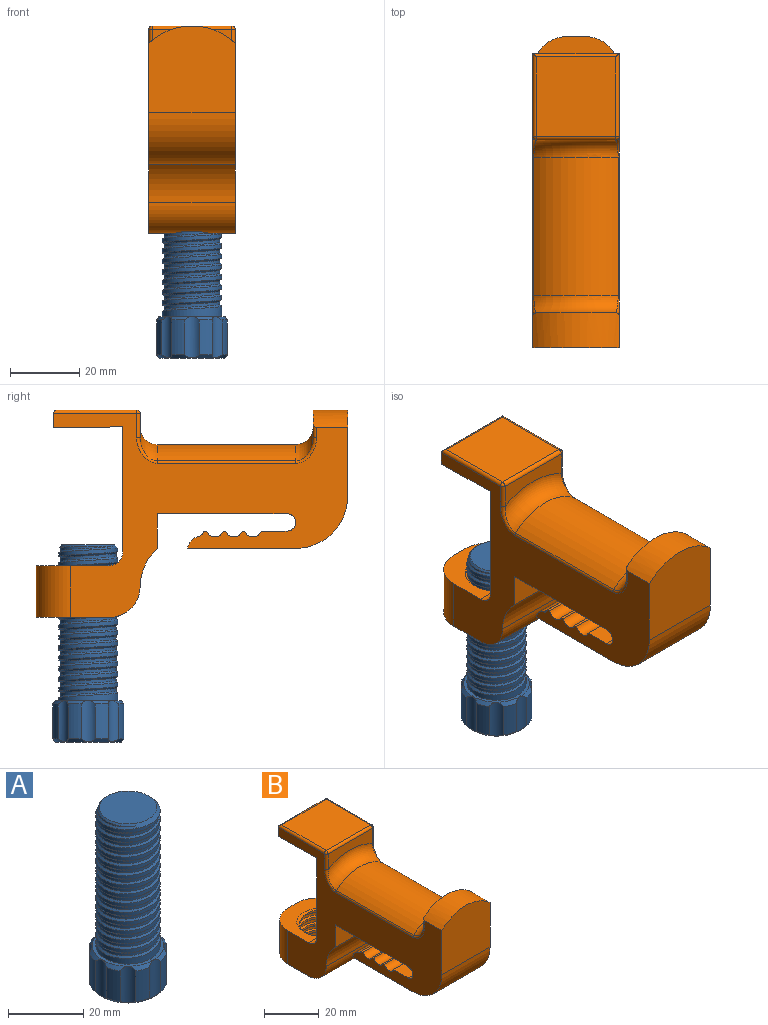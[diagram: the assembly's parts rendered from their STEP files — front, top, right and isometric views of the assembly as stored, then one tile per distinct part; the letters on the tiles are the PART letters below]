
ASSEMBLY  parts=2 mates=1
PART A: 41 faces, bbox 20.9x20.9x57.4 mm
  f0: cylinder r=10.45mm len=10mm, axis (0,0,-1), area 41mm2, adj f7,f27,f33,f40
  f1: cylinder r=10.45mm len=10mm, axis (0,0,-1), area 41mm2, adj f8,f14,f39,f40
  f2: cylinder r=10.45mm len=10mm, axis (0,0,-1), area 41mm2, adj f9,f15,f38,f39
  f3: cylinder r=10.45mm len=10mm, axis (0,0,-1), area 41mm2, adj f10,f16,f37,f38
  f4: cylinder r=10.45mm len=10mm, axis (0,0,-1), area 41mm2, adj f11,f17,f36,f37
  f5: cylinder r=10.45mm len=10mm, axis (0,0,-1), area 41mm2, adj f12,f18,f35,f36
  f6: cylinder r=10.45mm len=10mm, axis (0,0,-1), area 41mm2, adj f13,f19,f34,f35
  f7: cone r=10.45mm half-angle=43.5deg, axis (0,0,1), area 7mm2, adj f0,f24,f33,f40
  f8: cone r=10.45mm half-angle=43.5deg, axis (0,0,1), area 7mm2, adj f1,f24,f39,f40
  f9: cone r=10.45mm half-angle=43.5deg, axis (0,0,1), area 7mm2, adj f2,f24,f38,f39
  f10: cone r=10.45mm half-angle=43.5deg, axis (0,0,1), area 7mm2, adj f3,f24,f37,f38
  f11: cone r=10.45mm half-angle=43.5deg, axis (0,0,1), area 7mm2, adj f4,f24,f36,f37
  f12: cone r=10.45mm half-angle=43.5deg, axis (0,0,1), area 7mm2, adj f5,f24,f35,f36
  f13: cone r=10.45mm half-angle=43.5deg, axis (0,0,1), area 7mm2, adj f6,f24,f34,f35
  f14: cone r=10.45mm half-angle=43.5deg, axis (0,0,-1), area 7mm2, adj f1,f23,f39,f40
  f15: cone r=10.45mm half-angle=43.5deg, axis (0,0,-1), area 7mm2, adj f2,f23,f38,f39
  f16: cone r=10.45mm half-angle=43.5deg, axis (0,0,-1), area 7mm2, adj f3,f23,f37,f38
  f17: cone r=10.45mm half-angle=43.5deg, axis (0,0,-1), area 7mm2, adj f4,f23,f36,f37
  f18: cone r=10.45mm half-angle=43.5deg, axis (0,0,-1), area 7mm2, adj f5,f23,f35,f36
  f19: cone r=10.45mm half-angle=43.5deg, axis (0,0,-1), area 7mm2, adj f6,f23,f34,f35
  f20: cone r=10.45mm half-angle=43.5deg, axis (0,0,-1), area 7mm2, adj f22,f23,f33,f34
  f21: cylinder r=8.55mm len=44mm, axis (0,0,-1), area 1043.1mm2, adj f23,f28,f29,f30,f31
  f22: cylinder r=10.45mm len=10mm, axis (0,0,-1), area 41mm2, adj f20,f26,f33,f34
  f23: plane 19x19mm, normal (0,0,1), area 53.9mm2, adj f14,f15,f16,f17,f18,f19,f20,f21
  f24: plane 19x19mm, normal (0,0,-1), area 283.5mm2, adj f7,f8,f9,f10,f11,f12,f13,f26
  f25: plane 15.2x15.2mm, normal (0,0,1), area 181.5mm2, adj f28
  f26: cone r=10.45mm half-angle=43.5deg, axis (0,0,1), area 7mm2, adj f22,f24,f33,f34
  f27: cone r=10.45mm half-angle=43.5deg, axis (0,0,-1), area 7mm2, adj f0,f23,f33,f40
  f28: cone r=8.55mm half-angle=43.5deg, axis (0,0,-1), area 53.4mm2, adj f21,f25,f30,f31,f32
  f29: plane 1.88x0.48mm, normal (0,1,0), area 0.7mm2, adj f21,f30,f31,f32
  f30: bspline ~44.5x19.75mm, area 531.5mm2, adj f21,f28,f29,f32
  f31: bspline ~44x19.75mm, area 509.7mm2, adj f21,f28,f29,f32
  f32: cylinder r=8.08mm len=44mm, axis (0,0,-1), area 187.7mm2, adj f28,f29,f30,f31
  f33: cylinder r=3.15mm len=12mm, axis (0,0,-1), area 50.2mm2, adj f0,f7,f20,f22,f26,f27
  f34: cylinder r=3.15mm len=12mm, axis (0,0,-1), area 50.2mm2, adj f6,f13,f19,f20,f22,f26
  f35: cylinder r=3.15mm len=12mm, axis (0,0,-1), area 50.2mm2, adj f5,f6,f12,f13,f18,f19
  f36: cylinder r=3.15mm len=12mm, axis (0,0,-1), area 50.2mm2, adj f4,f5,f11,f12,f17,f18
  f37: cylinder r=3.15mm len=12mm, axis (0,0,-1), area 50.2mm2, adj f3,f4,f10,f11,f16,f17
  f38: cylinder r=3.15mm len=12mm, axis (0,0,-1), area 50.2mm2, adj f2,f3,f9,f10,f15,f16
  f39: cylinder r=3.15mm len=12mm, axis (0,0,-1), area 50.2mm2, adj f1,f2,f8,f9,f14,f15
  f40: cylinder r=3.15mm len=12mm, axis (0,0,-1), area 50.2mm2, adj f0,f1,f7,f8,f14,f27
PART B: 69 faces, bbox 38.8x90x61.2 mm
  f0: plane 25x21mm, normal (0,0,-1), area 248.9mm2, adj f3,f4,f10,f11,f23,f53,f54,f55
  f1: plane 25x21mm, normal (0,0,1), area 248.9mm2, adj f2,f6,f10,f11,f23,f53,f54,f55
  f2: cylinder r=4mm len=25mm, axis (1,0,0), area 131.3mm2, adj f1,f7,f10,f11,f24,f55,f57,f64
  f3: cylinder r=9mm len=25mm, axis (-1,0,0), area 319mm2, adj f0,f5,f10,f11,f50,f55,f57
  f4: cone r=9mm half-angle=45deg, axis (0,0,-1), area 12.5mm2, adj f0,f5,f56
  f5: bspline ~11.32x3.88mm, area 10.7mm2, adj f3,f4,f56,f57,f61,f63
  f6: cone r=8mm half-angle=45deg, axis (0,0,1), area 22.4mm2, adj f1,f7,f56,f57,f62
  f7: bspline ~4.4x2.44mm, area 2mm2, adj f2,f6,f57,f64
  f8: plane 23x8.06mm, normal (0,1,0), area 107.9mm2, adj f30,f31,f33,f48
  f9: plane 25x25mm, normal (0,-1,0), area 585.9mm2, adj f10,f11,f30,f49
  f10: plane 85.01x59mm, normal (1,0,0), area 1859.8mm2, adj f0,f1,f2,f3,f9,f12,f13,f14
  f11: plane 85.01x59mm, normal (-1,0,0), area 1859.8mm2, adj f0,f1,f2,f3,f9,f12,f13,f14
  f12: plane 31.26x25mm, normal (0,0,-1), area 781.6mm2, adj f10,f11,f49,f51
  f13: cylinder r=2.5mm len=25mm, axis (-1,0,0), area 63mm2, adj f10,f11,f14,f51
  f14: plane 25x0.75mm, normal (0,0,1), area 18.7mm2, adj f10,f11,f13,f15
  f15: cylinder r=2.5mm len=25mm, axis (-1,0,0), area 156.9mm2, adj f10,f11,f14,f16
  f16: plane 25x0.75mm, normal (0,0,1), area 18.7mm2, adj f10,f11,f15,f17
  f17: cylinder r=2.5mm len=25mm, axis (-1,0,0), area 156.9mm2, adj f10,f11,f16,f18
  f18: plane 25x0.75mm, normal (0,0,1), area 18.7mm2, adj f10,f11,f17,f19
  f19: cylinder r=2.5mm len=25mm, axis (-1,0,0), area 156.9mm2, adj f10,f11,f18,f20
  f20: plane 25x7.5mm, normal (0,0,1), area 187.5mm2, adj f10,f11,f19,f52
  f21: plane 37.5x25mm, normal (0,0,-1), area 937.5mm2, adj f10,f11,f22,f52
  f22: plane 25x10mm, normal (0,-1,0), area 250mm2, adj f10,f11,f21,f50
  f23: plane 15x5mm, normal (0,1,0), area 75mm2, adj f0,f1,f53,f54
  f24: plane 36.15x25mm, normal (0,1,0), area 903.7mm2, adj f2,f10,f11,f25
  f25: plane 25x20.01mm, normal (0,-0.02,-1), area 500.3mm2, adj f10,f11,f24,f26
  f26: plane 25x4.2mm, normal (0,1,0), area 105mm2, adj f10,f11,f25,f39
  f27: plane 23.01x23mm, normal (0,0,1), area 529.2mm2, adj f37,f39,f41,f42
  f28: plane 23x7.06mm, normal (0,-1,0), area 114.8mm2, adj f32,f38,f42,f44
  f29: cylinder r=18.12mm len=40mm, axis (0,1,0), area 1067.6mm2, adj f31,f32,f35,f46
  f30: cylinder r=18.12mm len=25mm, axis (0,-1,0), area 274.5mm2, adj f8,f9,f10,f11,f33,f48
  f31: torus R=23.12mm, axis (0,-1,0), area 195.4mm2, adj f8,f29,f34,f47
  f32: torus R=23.12mm, axis (0,-1,0), area 195.4mm2, adj f28,f29,f36,f45
  f33: cylinder r=1mm len=3.95mm, axis (0,0,-1), area 5.5mm2, adj f8,f10,f30,f34
  f34: bspline ~9.04x7.12mm, area 11.2mm2, adj f10,f31,f33,f35
  f35: cylinder r=1mm len=40mm, axis (0,1,0), area 33.4mm2, adj f10,f29,f34,f36
  f36: bspline ~9.04x7.12mm, area 11.2mm2, adj f10,f32,f35,f38
  f37: cylinder r=1mm len=24.01mm, axis (0,1,0), area 36.9mm2, adj f10,f27,f39,f40
  f38: cylinder r=1mm len=7.06mm, axis (0,0,1), area 11.1mm2, adj f10,f28,f36,f40
  f39: cylinder r=1mm len=25mm, axis (-1,0,0), area 37.7mm2, adj f26,f27,f37,f41
  f40: sphere r=1mm, area 1.6mm2, adj f37,f38,f42
  f41: cylinder r=1mm len=24.01mm, axis (0,-1,0), area 36.9mm2, adj f11,f27,f39,f43
  f42: cylinder r=1mm len=23mm, axis (-1,0,0), area 36.1mm2, adj f27,f28,f40,f43
  f43: sphere r=1mm, area 1.6mm2, adj f41,f42,f44
  f44: cylinder r=1mm len=7.06mm, axis (0,0,-1), area 11.1mm2, adj f11,f28,f43,f45
  f45: bspline ~9.04x7.12mm, area 11.2mm2, adj f11,f32,f44,f46
  f46: cylinder r=1mm len=40mm, axis (0,1,0), area 33.4mm2, adj f11,f29,f45,f47
  f47: bspline ~9.04x7.12mm, area 11.2mm2, adj f11,f31,f46,f48
  f48: cylinder r=1mm len=3.95mm, axis (0,0,1), area 5.5mm2, adj f8,f11,f30,f47
  f49: cylinder r=15mm len=25mm, axis (-1,0,0), area 589mm2, adj f9,f10,f11,f12
  f50: cylinder r=15mm len=25mm, axis (-1,0,0), area 312.4mm2, adj f3,f10,f11,f22
  f51: cylinder r=4mm len=25mm, axis (-1,0,0), area 119.2mm2, adj f10,f11,f12,f13
  f52: cylinder r=2.5mm len=25mm, axis (-1,0,0), area 196.3mm2, adj f10,f11,f20,f21
  f53: cylinder r=10mm len=15mm, axis (0,0,1), area 235.6mm2, adj f0,f1,f11,f23
  f54: cylinder r=10mm len=15mm, axis (0,0,-1), area 235.6mm2, adj f0,f1,f10,f23
  f55: cylinder r=9mm len=18mm, axis (0,0,-1), area 318.7mm2, adj f0,f1,f2,f3,f56,f57
  f56: bspline ~18x17.98mm, area 182.9mm2, adj f0,f1,f4,f5,f6,f55,f58,f59
  f57: bspline ~20.78x18mm, area 191mm2, adj f2,f3,f5,f6,f7,f55,f58,f59
  f58: cylinder r=8.5mm len=17mm, axis (0,0,-1), area 42.4mm2, adj f56,f57,f65,f66
  f59: cylinder r=8.5mm len=17mm, axis (0,0,-1), area 42.4mm2, adj f56,f57,f66,f67
  f60: cylinder r=8.5mm len=17mm, axis (0,0,-1), area 42.4mm2, adj f56,f57,f67,f68
  f61: cylinder r=8.5mm len=17mm, axis (0,0,-1), area 29.1mm2, adj f5,f56,f57,f68
  f62: cylinder r=8.5mm len=17mm, axis (0,0,-1), area 36.3mm2, adj f6,f56,f57,f65
  f63: cylinder r=8.5mm len=1.28mm, axis (0,0,-1), area 0mm2, adj f5,f56
  f64: cylinder r=8.5mm len=7.73mm, axis (0,0,-1), area 2mm2, adj f2,f7,f57
  f65: cylinder r=8mm len=4.62mm, axis (0,0,1), area 4.3mm2, adj f56,f57,f58,f62
  f66: cylinder r=8mm len=4.62mm, axis (0,0,1), area 4.3mm2, adj f56,f57,f58,f59
  f67: cylinder r=8mm len=4.62mm, axis (0,0,1), area 4.3mm2, adj f56,f57,f59,f60
  f68: cylinder r=8mm len=4.62mm, axis (0,0,1), area 4.3mm2, adj f56,f57,f60,f61
PLACE A t=(12.5,33.26,-70.44)mm
PLACE B at identity
MATE planar A.f32 <-> B.f4  axis (0,0,1) through (12.5,33.26,-13.44)mm
